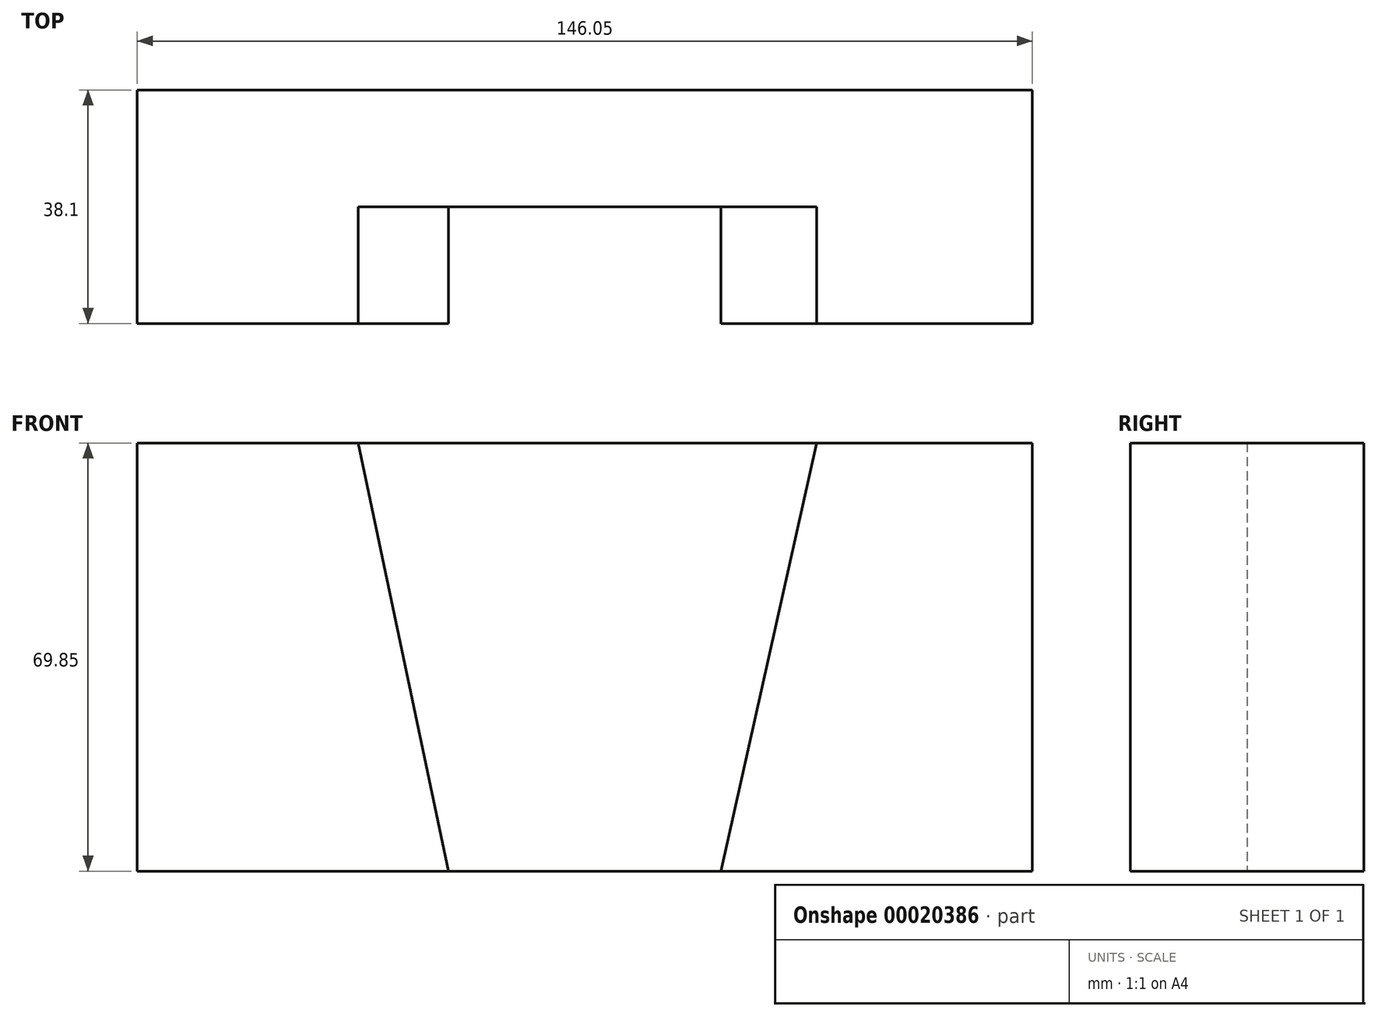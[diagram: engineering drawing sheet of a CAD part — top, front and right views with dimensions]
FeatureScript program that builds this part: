
annotation { "Feature Type Name" : "Feature", "Feature Type Description" : "" }
export const myFeature = defineFeature(function(context is Context, id is Id, definition is map)
    precondition{}
    {
        {
            var Q0;
            Q0=qCreatedBy(makeId("Front.planeOp"),FACE);
            var sketch = newSketch(context, id + "F0", { "sketchPlane" : qUnion([Q0])});
            skLineSegment(sketch, "E0.bottom", {"start": v(-74.83, 17.84) * mm, "end": v(71.22, 17.84) * mm});
            skLineSegment(sketch, "E0.top", {"start": v(-74.83, -52.01) * mm, "end": v(71.22, -52.01) * mm});
            skLineSegment(sketch, "E0.left", {"start": v(-74.83, 17.84) * mm, "end": v(-74.83, -52.01) * mm});
            skLineSegment(sketch, "E0.right", {"start": v(71.22, 17.84) * mm, "end": v(71.22, -52.01) * mm});
            skSolve(sketch);
        }
        {
            var Q0;
            Q0=makeQuery(id+"F0.imprint","IMPRINT",FACE,{"disambiguationData":[TD([[makeQuery(id+"F0.imprint","IMPRINT",EDGE,{"derivedFrom":sQuery(id+"F0.wireOp",EDGE,"E0.bottom")}),-1.0]])]});
            extrude(context, id + "F1", {"entities" : qUnion([Q0]), "depth" : 38.1 * mm});
        }
        {
            var Q0;
            Q0=makeQuery(id+"F1.opExtrude","CAP_FACE",FACE,{"disambiguationData":[OSD([sQuery(id+"F0.wireOp",EDGE,"E0.bottom"),sQuery(id+"F0.wireOp",EDGE,"E0.top"),sQuery(id+"F0.wireOp",EDGE,"E0.left"),sQuery(id+"F0.wireOp",EDGE,"E0.right")])],"isStart":false});
            var sketch = newSketch(context, id + "F2", { "sketchPlane" : qUnion([Q0])});
            skLineSegment(sketch, "E1", {"start": v(-74.83, -52.01) * mm, "end": v(-24.03, -52.01) * mm});
            skLineSegment(sketch, "E2", {"start": v(71.22, -52.01) * mm, "end": v(20.42, -52.01) * mm});
            skLineSegment(sketch, "E3", {"start": v(-38.8, 17.84) * mm, "end": v(-24.03, -52.01) * mm});
            skLineSegment(sketch, "E4", {"start": v(36.04, 17.84) * mm, "end": v(20.42, -52.01) * mm});
            skSolve(sketch);
        }
        {
            var Q0;
            {var subQ2=sQuery(id+"F2.wireOp",EDGE,"E3");Q0=makeQuery(id+"F2.imprint","IMPRINT",FACE,{"disambiguationData":[TD([[makeQuery(id+"F2.imprint","IMPRINT",EDGE,{"derivedFrom":subQ2}),1.0]])]});}
            extrude(context, id + "F3", {"entities" : qUnion([Q0]), "operationType" : NewBodyOperationType.REMOVE, "oppositeDirection" : true, "depth" : 19.05 * mm});
        }
    });
